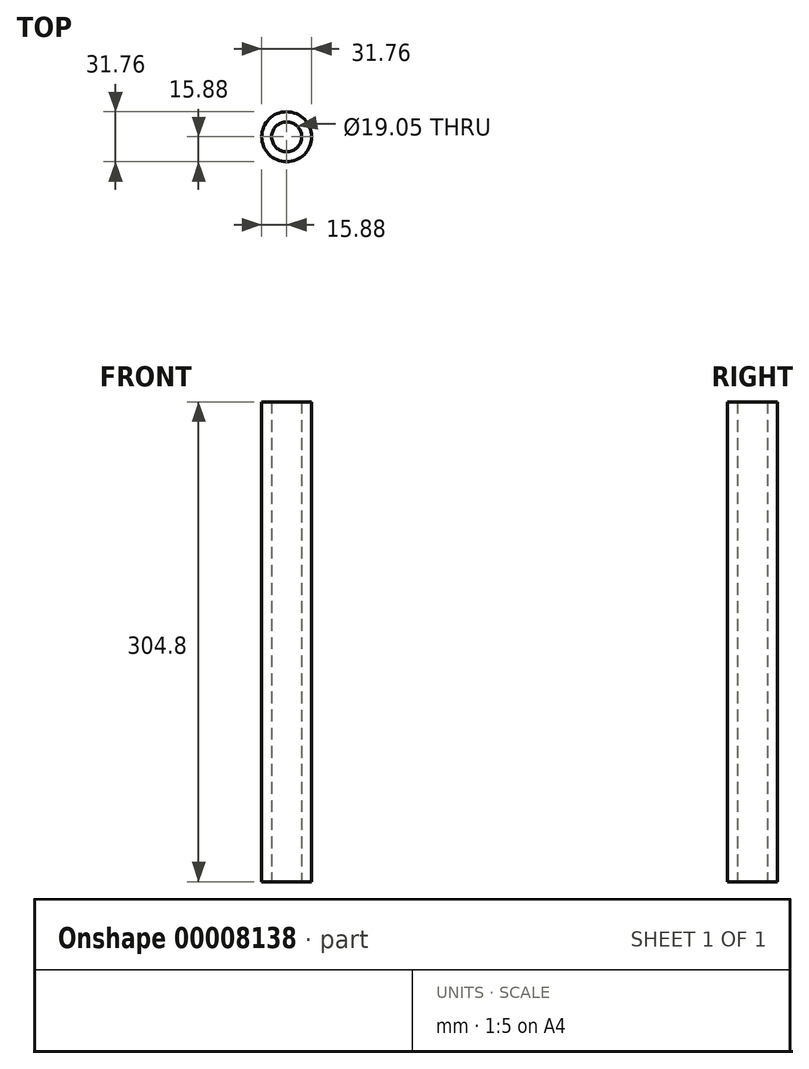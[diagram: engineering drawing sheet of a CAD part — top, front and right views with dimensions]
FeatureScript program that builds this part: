
annotation { "Feature Type Name" : "Feature", "Feature Type Description" : "" }
export const myFeature = defineFeature(function(context is Context, id is Id, definition is map)
    precondition{}
    {
        {
            var Q0;
            Q0=qCreatedBy(makeId("Top.planeOp"),FACE);
            var sketch = newSketch(context, id + "F0", { "sketchPlane" : qUnion([Q0])});
            skCircle(sketch, "E0", {"center": v(0, 0) * mm, "radius": 15.88 * mm});
            skCircle(sketch, "E1", {"center": v(0, 0) * mm, "radius": 9.53 * mm});
            skSolve(sketch);
        }
        {
            var Q0;
            Q0=makeQuery(id+"F0.imprint","IMPRINT",FACE,{"disambiguationData":[TD([[makeQuery(id+"F0.imprint","IMPRINT",EDGE,{"derivedFrom":sQuery(id+"F0.wireOp",EDGE,"E0")}),1.0]])]});
            extrude(context, id + "F1", {"entities" : qUnion([Q0]), "depth" : 304.8 * mm});
        }
    });
